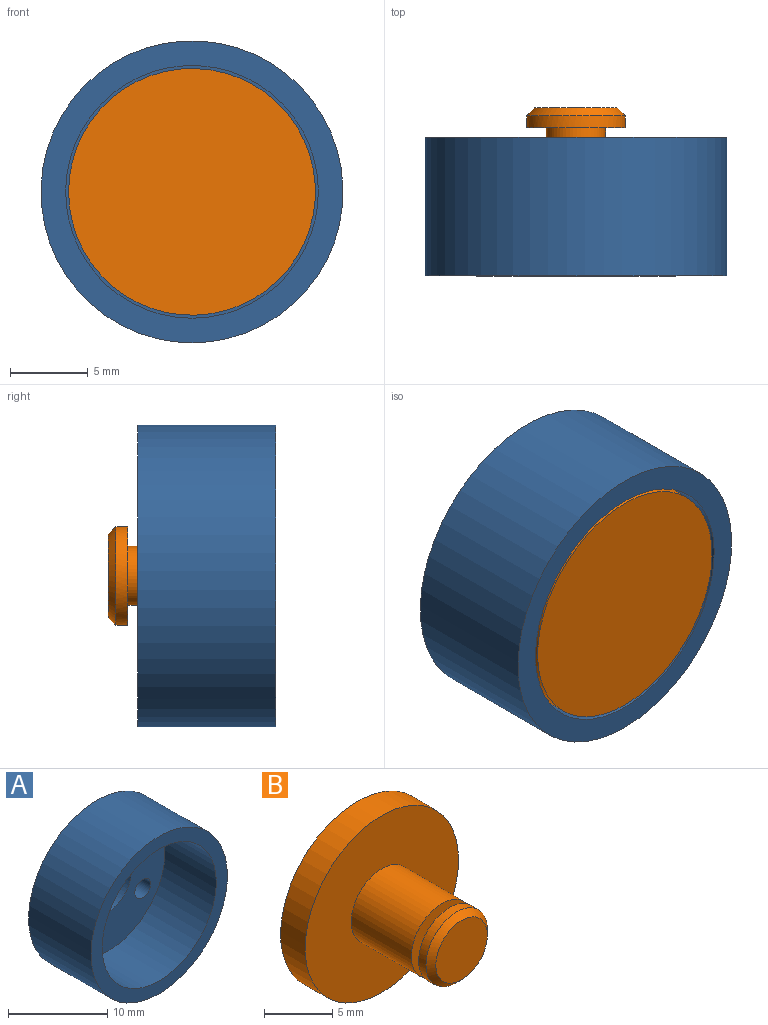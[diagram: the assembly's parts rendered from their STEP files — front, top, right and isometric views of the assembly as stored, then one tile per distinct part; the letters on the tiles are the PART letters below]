
ASSEMBLY  parts=2 mates=1
PART A: 9 faces, bbox 19.4x8.9x19.4 mm
  f0: cylinder r=8.13mm len=16.26mm, axis (0,1,0), area 372.9mm2, adj f2,f4
  f1: cylinder r=9.72mm len=19.43mm, axis (0,1,0), area 542.7mm2, adj f2,f3
  f2: plane 19.43x19.43mm, normal (0,-1,0), area 89mm2, adj f0,f1
  f3: plane 19.43x19.43mm, normal (0,1,0), area 250.2mm2, adj f1,f5,f6,f7,f8
  f4: plane 16.26x16.26mm, normal (0,-1,0), area 161.3mm2, adj f0,f5,f6,f7,f8
  f5: cylinder r=3.3mm len=6.6mm, axis (0,-1,0), area 32.9mm2, adj f3,f4
  f6: cylinder r=1.13mm len=2.26mm, axis (0,-1,0), area 11.3mm2, adj f3,f4
  f7: cylinder r=1.13mm len=2.26mm, axis (0,-1,0), area 11.3mm2, adj f3,f4
  f8: cylinder r=1.13mm len=2.26mm, axis (0,-1,0), area 11.3mm2, adj f3,f4
PART B: 10 faces, bbox 15.9x10.8x15.9 mm
  f0: cylinder r=3.17mm len=6.35mm, axis (0,1,0), area 124.1mm2, adj f2,f5
  f1: cylinder r=7.94mm len=15.88mm, axis (0,1,0), area 126.7mm2, adj f2,f3
  f2: plane 15.88x15.88mm, normal (0,-1,0), area 166.3mm2, adj f0,f1
  f3: plane 15.88x15.88mm, normal (0,1,0), area 197.9mm2, adj f1
  f4: plane 6.35x6.35mm, normal (0,1,0), area 20.3mm2, adj f6,f8
  f5: plane 6.35x6.35mm, normal (0,-1,0), area 20.3mm2, adj f0,f6
  f6: cylinder r=1.91mm len=3.81mm, axis (0,-1,0), area 9.1mm2, adj f4,f5
  f7: plane 5.33x5.33mm, normal (0,-1,0), area 22.3mm2, adj f9
  f8: cylinder r=3.17mm len=6.35mm, axis (0,1,0), area 15.2mm2, adj f4,f9
  f9: cone r=2.67mm half-angle=45deg, axis (0,1,0), area 13.2mm2, adj f7,f8
PLACE A at identity fixed
PLACE B rot(axis=(0.71,0,0.71),180deg) t=(0,-8.89,0)mm
MATE revolute B.f6 <-> A.f5  axis (0,-1,0) through (0,0.64,0)mm
